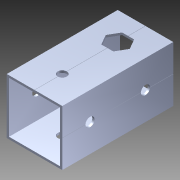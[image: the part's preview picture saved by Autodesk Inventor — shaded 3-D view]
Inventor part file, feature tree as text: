
AUTODESK INVENTOR PART (.ipt)
format: ipt  version: 2014 SP1 (Build 180222100, 222)  size: 1,168,384 bytes
history: native  units: in
note: dims shown in document units (in); Inventor stores cm internally (conversion verified against a paired STEP export)
features: extrude x2, sketch x2, pattern_circular x1, other x1, plane x1, imported_body x1
ambient origin geometry x8: Origin, YZ Plane, XZ Plane, XY Plane, X Axis, Y Axis, Z Axis, Center Point
bodies: Body1 (feature_tree)
feature tree (8):
  pattern_circular  "CirPattern2"
  other  "217-3426-STEP1"
  plane  "Work Plane1"
  extrude  "Extrusion1"  Depth=3937.0079in TaperAngle=0.0deg
  extrude  "Extrusion2"  Depth=2.0in TaperAngle=0.0deg
  imported_body  "Base1"
  sketch  "Sketch1"  dims[d0=-2.0in d1=3937.0079in d2=0.0in]
  sketch  "Sketch3"  dims[d3=0.375in d4=2.0in d5=0.0in]
